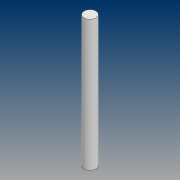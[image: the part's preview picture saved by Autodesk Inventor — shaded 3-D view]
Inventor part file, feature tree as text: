
AUTODESK INVENTOR PART (.ipt)
format: ipt  version: 2021 (Build 250183000, 183)  size: 73,728 bytes
history: native  units: mm
features: extrude x1, sketch x1
ambient origin geometry x8: Origin, YZ Plane, XZ Plane, XY Plane, X Axis, Y Axis, Z Axis, Center Point
bodies: Solid1 (feature_tree)
feature tree (2):
  extrude  "Extrusion1"  Depth=110.0mm TaperAngle=0.0deg
  sketch  "Sketch1"  dims[d0=10.0mm d1=110.0mm d2=0.0mm]
